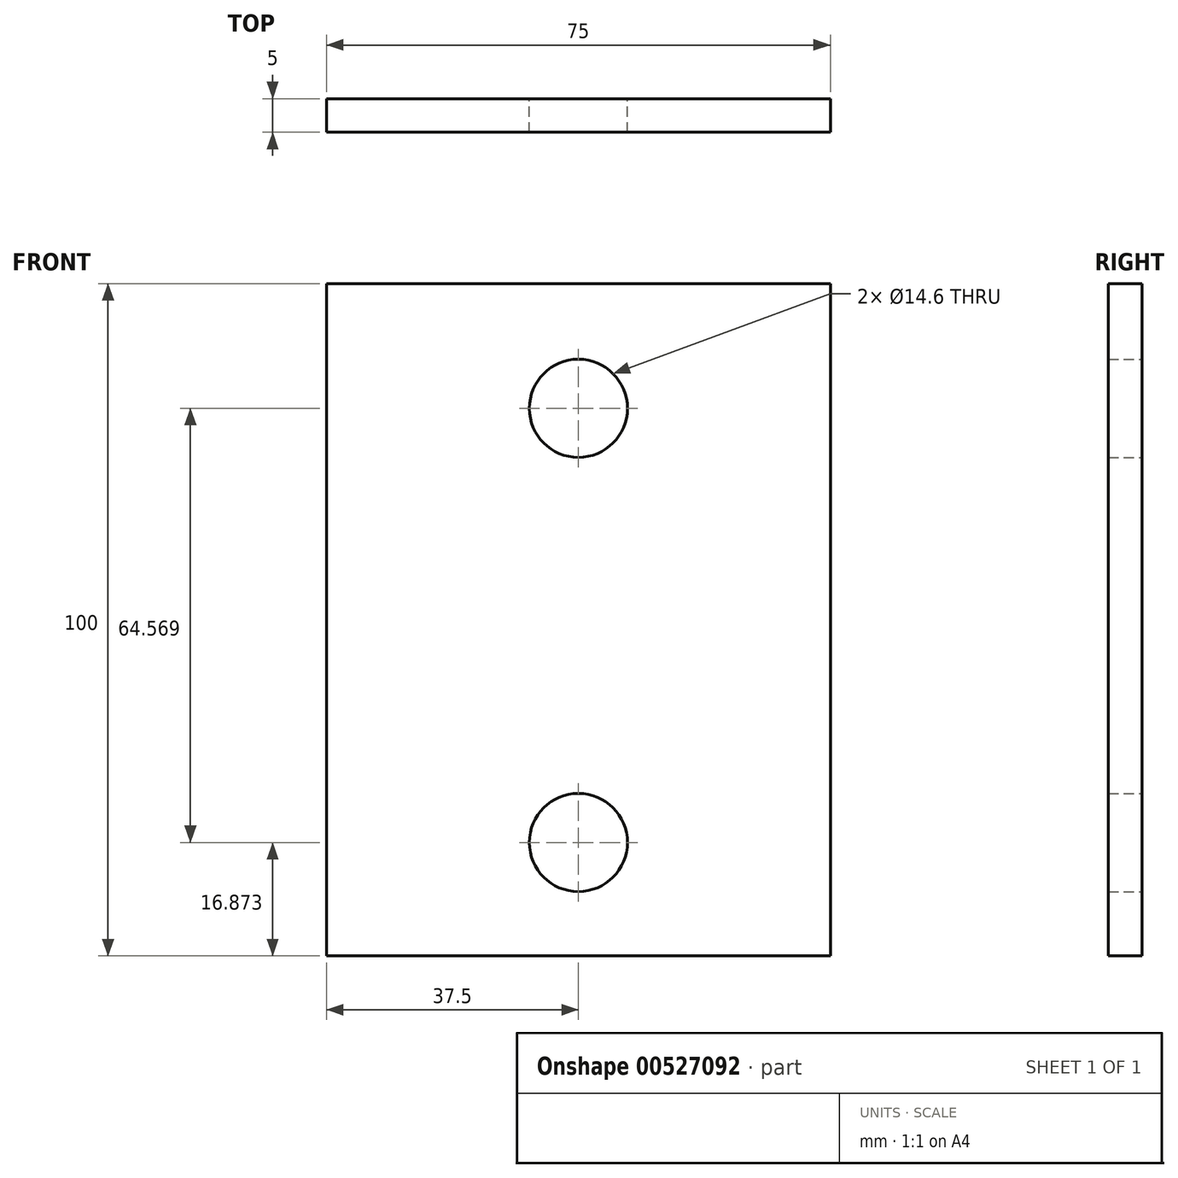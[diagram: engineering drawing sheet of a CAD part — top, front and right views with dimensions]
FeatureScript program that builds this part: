
annotation { "Feature Type Name" : "Feature", "Feature Type Description" : "" }
export const myFeature = defineFeature(function(context is Context, id is Id, definition is map)
    precondition{}
    {
        {
            var Q0;
            Q0=qCreatedBy(makeId("Front.planeOp"),FACE);
            var sketch = newSketch(context, id + "F0", { "sketchPlane" : qUnion([Q0])});
            skLineSegment(sketch, "E0.bottom", {"start": v(37.5, -50) * mm, "end": v(-37.5, -50) * mm});
            skLineSegment(sketch, "E0.top", {"start": v(37.5, 50) * mm, "end": v(-37.5, 50) * mm});
            skLineSegment(sketch, "E0.left", {"start": v(37.5, -50) * mm, "end": v(37.5, 50) * mm});
            skLineSegment(sketch, "E0.right", {"start": v(-37.5, -50) * mm, "end": v(-37.5, 50) * mm});
            skCircle(sketch, "E1", {"center": v(0, 31.44) * mm, "radius": 7.3 * mm});
            skCircle(sketch, "E2", {"center": v(0, -33.13) * mm, "radius": 7.3 * mm});
            skSolve(sketch);
        }
        {
            var Q0;
            Q0=makeQuery(id+"F0.imprint","IMPRINT",FACE,{"disambiguationData":[TD([[makeQuery(id+"F0.imprint","IMPRINT",EDGE,{"derivedFrom":sQuery(id+"F0.wireOp",EDGE,"E0.bottom")}),-1.0]])]});
            extrude(context, id + "F1", {"entities" : qUnion([Q0]), "depth" : 5 * mm, "offsetDistance" : 25.4 * mm});
        }
    });
